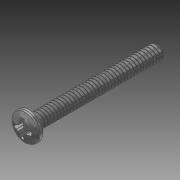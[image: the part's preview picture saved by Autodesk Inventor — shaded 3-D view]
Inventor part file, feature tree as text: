
AUTODESK INVENTOR PART (.ipt)
format: ipt  version: 2014 SP1 (Build 180222100, 222)  size: 1,003,008 bytes
history: native  units: in
note: dims shown in document units (in); Inventor stores cm internally (conversion verified against a paired STEP export)
features: fillet x1, other x1, imported_body x1
ambient origin geometry x8: Origin, YZ Plane, XZ Plane, XY Plane, X Axis, Y Axis, Z Axis, Center Point
bodies: Body1 (feature_tree)
feature tree (3):
  fillet  "Fillet1"  [1 undecoded]
  other  "91772A1551"
  imported_body  "Base1"
note: 1 required parameter value undecoded (feature->parameter linkage not recoverable at this tier; creation-order binding heuristic only, values carry confidence <= 0.55)
